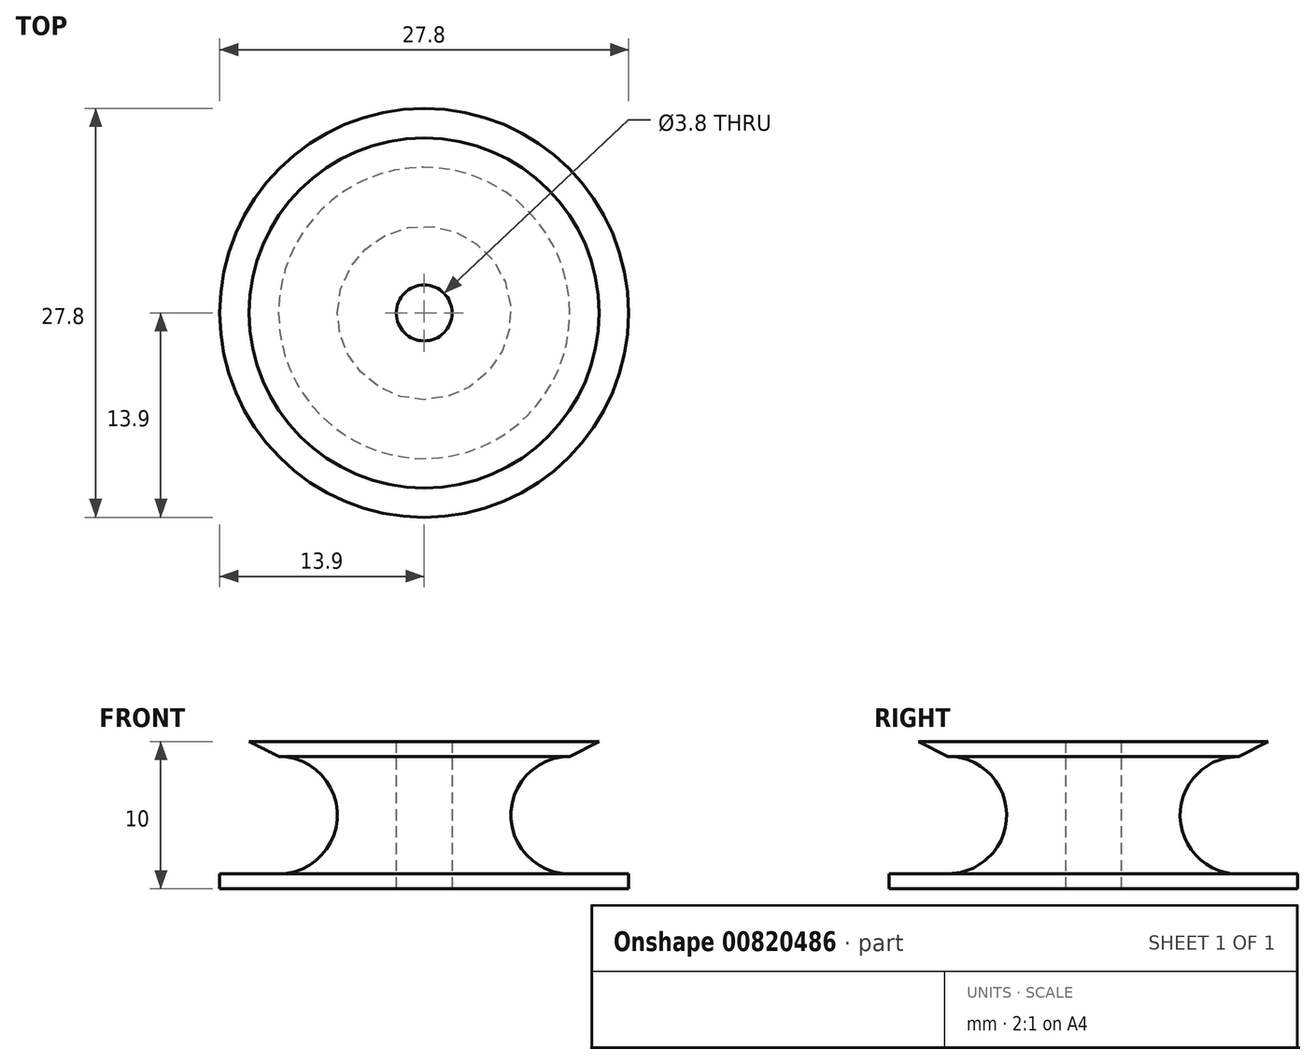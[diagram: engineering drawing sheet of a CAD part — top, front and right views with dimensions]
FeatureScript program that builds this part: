
annotation { "Feature Type Name" : "Feature", "Feature Type Description" : "" }
export const myFeature = defineFeature(function(context is Context, id is Id, definition is map)
    precondition{}
    {
        {
            var Q0;
            Q0=qCreatedBy(makeId("Right.planeOp"),FACE);
            var sketch = newSketch(context, id + "F0", { "sketchPlane" : qUnion([Q0])});
            skLineSegment(sketch, "E0", {"start": v(0, 0) * mm, "end": v(0, 5) * mm, "construction": true});
            skLineSegment(sketch, "E1", {"start": v(-1.9, 5) * mm, "end": v(-9.9, 5) * mm});
            skLineSegment(sketch, "E2", {"start": v(-9.9, 5) * mm, "end": v(-9.9, 4) * mm, "construction": true});
            skLineSegment(sketch, "E3", {"start": v(-1.9, 5) * mm, "end": v(-1.9, -5) * mm});
            skLineSegment(sketch, "E4", {"start": v(-1.9, -5) * mm, "end": v(-9.9, -5) * mm});
            skLineSegment(sketch, "E5", {"start": v(-9.9, -5) * mm, "end": v(-9.9, -4) * mm, "construction": true});
            skArc(sketch, "E6", {"start": v(-9.9, -4) * mm, "mid": v(-5.9, 0) * mm, "end": v(-9.9, 4) * mm});
            skLineSegment(sketch, "E7", {"start": v(-9.9, 5) * mm, "end": v(-11.9, 5) * mm});
            skLineSegment(sketch, "E8", {"start": v(-11.9, 5) * mm, "end": v(-9.9, 4) * mm});
            skLineSegment(sketch, "E9", {"start": v(-9.9, -5) * mm, "end": v(-13.9, -5) * mm});
            skLineSegment(sketch, "E10", {"start": v(-9.9, -4) * mm, "end": v(-13.9, -4) * mm});
            skLineSegment(sketch, "E11", {"start": v(-13.9, -4) * mm, "end": v(-13.9, -5) * mm});
            skSolve(sketch);
        }
        {
            var Q0;
            Q0=makeQuery(id+"F0.imprint","IMPRINT",FACE,{"disambiguationData":[TD([[makeQuery(id+"F0.imprint","IMPRINT",EDGE,{"derivedFrom":sQuery(id+"F0.wireOp",EDGE,"E1")}),1.0]])]});
            var Q1;
            Q1=sQuery(id+"F0.wireOp",EDGE,"E0");
            revolve(context, id + "F1", {"surfaceOperationType" : NewSurfaceOperationType.NEW, "entities" : qUnion([Q0]), "axis" : qUnion([Q1]), "revolveType" : RevolveType.FULL});
        }
    });
